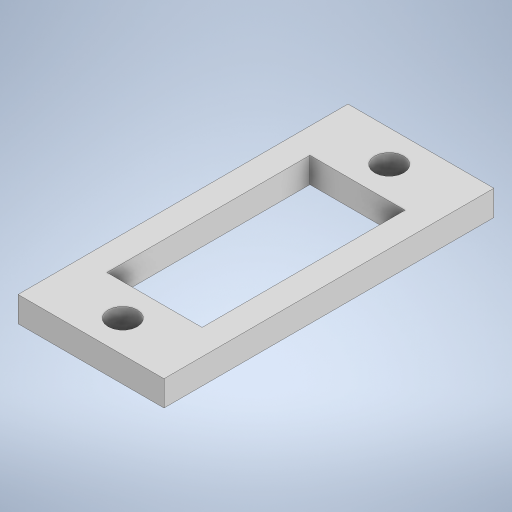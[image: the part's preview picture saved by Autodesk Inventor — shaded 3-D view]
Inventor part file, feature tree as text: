
AUTODESK INVENTOR PART (.ipt)
format: ipt  version: 2024.2 (Build 282272000, 272)  size: 235,008 bytes
history: native  units: mm
features: extrude x1, sketch x1
ambient origin geometry x8: Origin, YZ Plane, XZ Plane, XY Plane, X Axis, Y Axis, Z Axis, Center Point
bodies: Solid1 (feature_tree)
feature tree (2):
  extrude  "Extrusion1"  Depth=16.0mm
  sketch  "Sketch1"  dims[d0=7.5mm d1=16.0mm d2=2.0mm d3=2.0mm d4=5.0mm d5=5.0mm d6=2.3mm d7=2.3mm d8=2.5mm d9=2.5mm d10=3.75mm d11=2.0mm d12=0.0mm]
